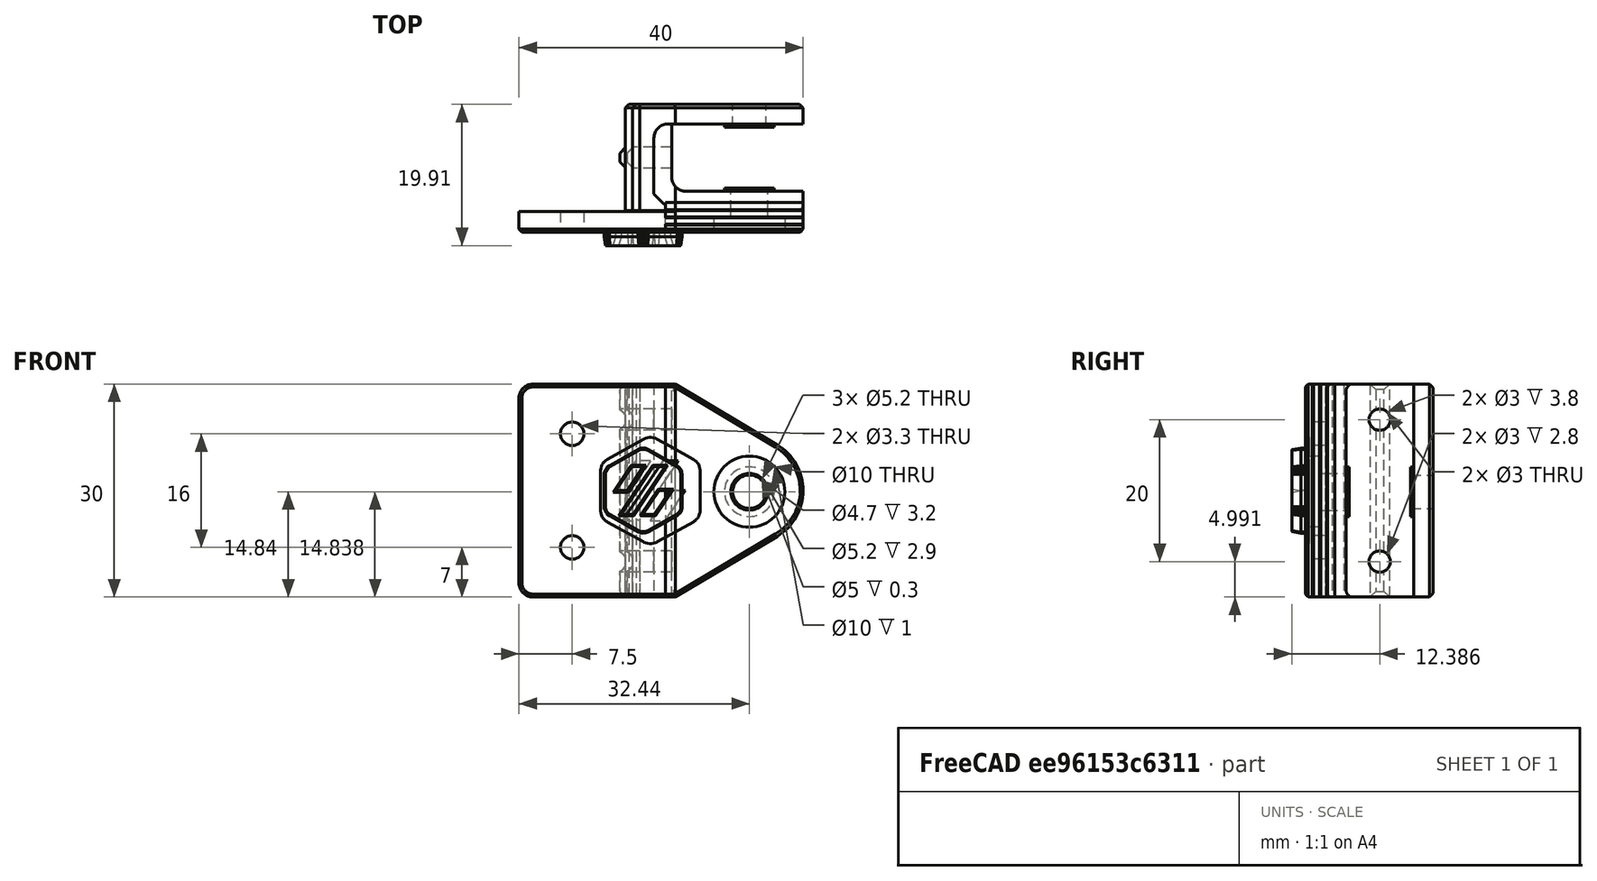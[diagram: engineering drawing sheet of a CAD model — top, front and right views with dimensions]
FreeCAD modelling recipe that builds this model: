
FCSTD DOCUMENT  (FreeCAD 0.18R16146 (Git))
Label: belt-z-idler-mount
License: All rights reserved
LicenseURL: http://en.wikipedia.org/wiki/All_rights_reserved
objects: Part::Cut×11, Part::Feature×10, Part::Box×7, Part::Cylinder×6, Part::MultiCommon×2, App::DocumentObjectGroup×2, Part::Chamfer×2, Part::Fillet×1, Part::MultiFuse×1
note: 40 computed .brp shape members not serialized (recipe doc carries the construction recipe); baked Part::Feature solids carry a one-line shape summary decoded from their .brp

FEATURE [Part::Box] Box  label="Cube"
  AttacherType = Attacher::AttachEngine3D
  Height = 40
  Length = 37
  Placement = pos=(-3,2,0) rot=(0,0,1;0rad)
  Width = 1.15
FEATURE [Part::Feature] Part__Feature018001  label="back"
  Placement = pos=(3,-4.85,-1.83) rot=(0,0,1;0rad)
  shape: bbox 24.8 x 15 x 30 mm, 38 faces (baked)
FEATURE [Part::Feature] Part__Feature016001  label="front"
  Placement = pos=(3,-1.85,-1.83) rot=(0,0,1;0rad)
  shape: bbox 21.62 x 12.25 x 30 mm, 26 faces (baked)
FEATURE [Part::Box] Box003  label="Cube003"
  AttacherType = Attacher::AttachEngine3D
  Height = 32
  Length = 10
  Placement = pos=(-7,0,0) rot=(0,0,1;0rad)
  Width = 17
FEATURE [Part::Feature] Part__Feature018003  label="back001"
  Placement = pos=(3,-4.85,-1.83) rot=(0,0,1;0rad)
  shape: bbox 24.8 x 15 x 30 mm, 38 faces (baked)
FEATURE [Part::MultiCommon] Common002
  Placement = pos=(-1,0,0) rot=(0,0,1;0rad)
  Shapes = -> [Part__Feature018003,Box003]
FEATURE [App::DocumentObjectGroup] Group  label="Back"
  Group = -> [Common002,Part__Feature018001]
FEATURE [Part::Feature] Part__Feature018004  label="front001"
  Placement = pos=(3,-1.85,-1.83) rot=(0,0,1;0rad)
  shape: bbox 21.62 x 12.25 x 30 mm, 26 faces (baked)
FEATURE [Part::MultiCommon] Common  label="add-front"
  Placement = pos=(0,-4,0) rot=(0,0,1;0rad)
  Shapes = -> [Box,Part__Feature018004]
FEATURE [Part::Feature] Common003  label="add-front001"
  Placement = pos=(0,-3,0) rot=(0,0,1;0rad)
  shape: bbox 20.75 x 1.15 x 30 mm, 9 faces (baked)
FEATURE [Part::Feature] Common004  label="add-front002"
  Placement = pos=(0,-2,0) rot=(0,0,1;0rad)
  shape: bbox 20.75 x 1.15 x 30 mm, 9 faces (baked)
FEATURE [Part::Feature] Common005  label="add-front003"
  Placement = pos=(0,-1,0) rot=(0,0,1;0rad)
  shape: bbox 20.75 x 1.15 x 30 mm, 9 faces (baked)
FEATURE [Part::Box] Box004  label="extend"
  AttacherType = Attacher::AttachEngine3D
  Height = 30
  Length = 22
  Placement = pos=(-15,-2,0) rot=(0,0,1;0rad)
  Width = 2.9
FEATURE [Part::Box] Box005  label="Cube005"
  AttacherType = Attacher::AttachEngine3D
  Height = 30
  Length = 22
  Placement = pos=(-16.4,-4.15,0) rot=(0,0,1;0rad)
  Width = 6.85
FEATURE [Part::Box] Box006  label="Cube006"
  AttacherType = Attacher::AttachEngine3D
  Height = 30
  Length = 22
  Placement = pos=(-16.4,-4.15,0) rot=(0,0,1;0rad)
  Width = 6.85
FEATURE [Part::Box] Box007  label="Cube007"
  AttacherType = Attacher::AttachEngine3D
  Height = 30
  Length = 22
  Placement = pos=(-16.4,-4.15,0) rot=(0,0,1;0rad)
  Width = 6.85
FEATURE [Part::Box] Box008  label="Cube008"
  AttacherType = Attacher::AttachEngine3D
  Height = 30
  Length = 22
  Placement = pos=(-16.4,-4.15,0) rot=(0,0,1;0rad)
  Width = 6.85
FEATURE [Part::Cut] Cut
  Base = -> Common
  Tool = -> Box005
FEATURE [Part::Cut] Cut001
  Base = -> Common003
  Tool = -> Box008
FEATURE [Part::Cut] Cut002
  Base = -> Common004
  Tool = -> Box007
FEATURE [Part::Cut] Cut003
  Base = -> Common005
  Tool = -> Box006
FEATURE [Part::Cylinder] Cylinder
  Angle = 360
  AttacherType = Attacher::AttachEngine3D
  Height = 10
  Placement = pos=(17.44,3.6e-15,14.84) rot=(1,0,0;1.5708rad)
  Radius = 5
FEATURE [Part::Cylinder] Cylinder001
  Angle = 360
  AttacherType = Attacher::AttachEngine3D
  Height = 10
  Placement = pos=(17.44,4e-15,14.84) rot=(1,0,0;1.5708rad)
  Radius = 5
FEATURE [Part::Cylinder] Cylinder002
  Angle = 360
  AttacherType = Attacher::AttachEngine3D
  Height = 10
  Placement = pos=(17.44,4e-15,14.84) rot=(1,0,0;1.5708rad)
  Radius = 5
FEATURE [Part::Cylinder] Cylinder003
  Angle = 360
  AttacherType = Attacher::AttachEngine3D
  Height = 10
  Placement = pos=(17.44,4e-15,14.84) rot=(1,0,0;1.5708rad)
  Radius = 5
FEATURE [Part::Cut] Cut004
  Base = -> Cut
  Tool = -> Cylinder
FEATURE [Part::Cut] Cut005
  Base = -> Cut003
  Tool = -> Cylinder003
FEATURE [Part::Cut] Cut006
  Base = -> Cut002
  Tool = -> Cylinder002
FEATURE [Part::Cut] Cut007
  Base = -> Cut001
  Tool = -> Cylinder001
FEATURE [Part::Fillet] Fillet
  Base = -> Box004
  Edges = 2 edges r=2: [Edge2,Edge4]
FEATURE [Part::Cylinder] Cylinder004
  Angle = 360
  AttacherType = Attacher::AttachEngine3D
  Height = 10
  Placement = pos=(-7.5,3,7) rot=(1,0,0;1.5708rad)
  Radius = 1.65
FEATURE [Part::Cylinder] Cylinder005
  Angle = 360
  AttacherType = Attacher::AttachEngine3D
  Height = 10
  Placement = pos=(-7.5,3,23) rot=(1,0,0;1.5708rad)
  Radius = 1.65
FEATURE [Part::MultiFuse] Fusion
  Shapes = -> [Cylinder005,Cylinder004]
FEATURE [Part::Cut] Cut008
  Base = -> Fillet
  Tool = -> Fusion
FEATURE [Part::Chamfer] Chamfer001
  Base = -> Cut004
  Edges = 5 edges r=0.4: [Edge1,Edge3,Edge4,Edge5,Edge6]
FEATURE [Part::Chamfer] Chamfer
  Base = -> Cut008
  Edges = 5 edges r=0.4: [Edge1,Edge5,Edge6,Edge8,Edge9]
FEATURE [Part::Feature] Exquisite_Curcan_Bombul001001_solid001  label="logo12"
  Placement = pos=(4,-1.5,14) rot=(1,0,0;1.5708rad)
  shape: bbox 11 x 2.413 x 12 mm, 187 faces (baked)
FEATURE [Part::Feature] Exquisite_Curcan_Bombul_2_001001_solid  label="Exquisite_Curcan_Bombul_2_002 (Solid)"
  Placement = pos=(3.5,-1.5,12.5) rot=(1,0,0;1.5708rad)
  shape: bbox 14 x 2.413 x 15 mm, 191 faces (baked)
FEATURE [Part::Feature] Exquisite_Curcan_Bombul_2_001001_solid001  label="Exquisite_Curcan_Bombul_2_002 (Solid)001"
  Placement = pos=(3.5,-1.5,12.5) rot=(1,0,0;1.5708rad)
  shape: bbox 14 x 2.413 x 15 mm, 191 faces (baked)
FEATURE [Part::Cut] Cut009
  Base = -> Chamfer
  Tool = -> Exquisite_Curcan_Bombul_2_001001_solid001
FEATURE [Part::Cut] Cut010
  Base = -> Chamfer001
  Tool = -> Exquisite_Curcan_Bombul_2_001001_solid
FEATURE [App::DocumentObjectGroup] Group001  label="front002"
  Group = -> [Cut007,Cut006,Cut005,Part__Feature016001,Cut009,Cut010]
